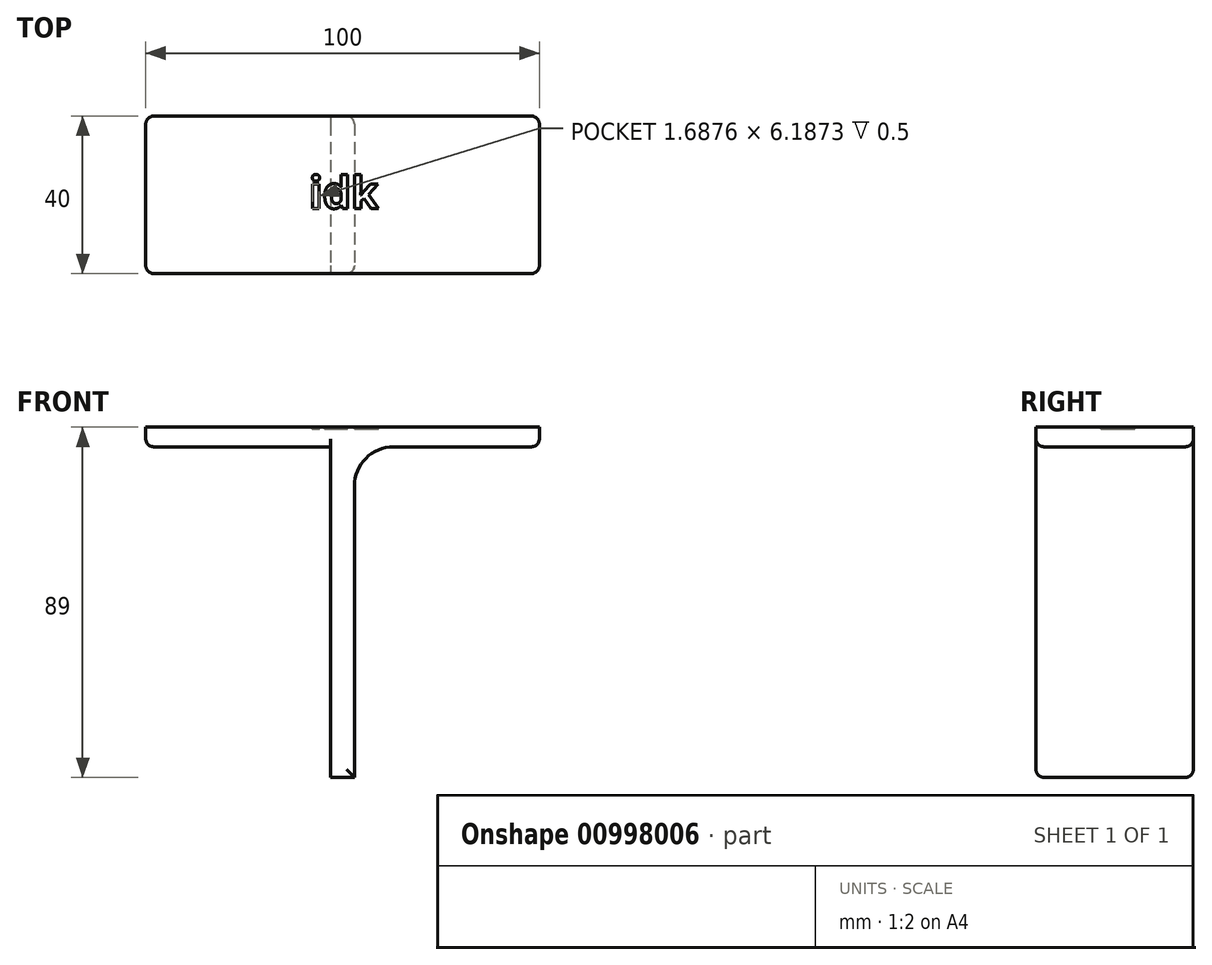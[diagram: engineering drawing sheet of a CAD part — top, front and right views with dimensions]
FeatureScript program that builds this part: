
annotation { "Feature Type Name" : "Feature", "Feature Type Description" : "" }
export const myFeature = defineFeature(function(context is Context, id is Id, definition is map)
    precondition{}
    {
        {
            var Q0;
            Q0=qCreatedBy(makeId("Top.planeOp"),FACE);
            var sketch = newSketch(context, id + "F0", { "sketchPlane" : qUnion([Q0])});
            skLineSegment(sketch, "E0.bottom", {"start": v(50, -20) * mm, "end": v(-50, -20) * mm});
            skLineSegment(sketch, "E0.top", {"start": v(50, 20) * mm, "end": v(-50, 20) * mm});
            skLineSegment(sketch, "E0.left", {"start": v(50, -20) * mm, "end": v(50, 20) * mm});
            skLineSegment(sketch, "E0.right", {"start": v(-50, -20) * mm, "end": v(-50, 20) * mm});
            skPoint(sketch, "E0.middle", {"position": v(0, 0) * mm});
            skLineSegment(sketch, "E1.bottom", {"start": v(-3, 20) * mm, "end": v(3, 20) * mm});
            skLineSegment(sketch, "E1.top", {"start": v(-3, -20) * mm, "end": v(3, -20) * mm});
            skLineSegment(sketch, "E1.left", {"start": v(-3, 20) * mm, "end": v(-3, -20) * mm});
            skLineSegment(sketch, "E1.right", {"start": v(3, 20) * mm, "end": v(3, -20) * mm});
            skSolve(sketch);
        }
        {
            var Q0;
            {var subQ2=sQuery(id+"F0.wireOp",EDGE,"E0.right");Q0=makeQuery(id+"F0.imprint","IMPRINT",FACE,{"disambiguationData":[TD([[makeQuery(id+"F0.imprint","IMPRINT",EDGE,{"derivedFrom":subQ2}),-1.0]])]});}
            var Q1;
            {var subQ0=sQuery(id+"F0.wireOp",EDGE,"E1.left");Q1=makeQuery(id+"F0.imprint","IMPRINT",FACE,{"disambiguationData":[TD([[makeQuery(id+"F0.imprint","IMPRINT",EDGE,{"derivedFrom":subQ0}),1.0]])]});}
            var Q2;
            {var subQ0=sQuery(id+"F0.wireOp",EDGE,"E0.left");Q2=makeQuery(id+"F0.imprint","IMPRINT",FACE,{"disambiguationData":[TD([[makeQuery(id+"F0.imprint","IMPRINT",EDGE,{"derivedFrom":subQ0}),1.0]])]});}
            extrude(context, id + "F1", {"entities" : qUnion([Q0, Q1, Q2]), "depth" : 5 * mm, "offsetDistance" : 25 * mm});
        }
        {
            var Q0;
            {var subQ0=sQuery(id+"F0.wireOp",EDGE,"E1.left");Q0=makeQuery(id+"F0.imprint","IMPRINT",FACE,{"disambiguationData":[TD([[makeQuery(id+"F0.imprint","IMPRINT",EDGE,{"derivedFrom":subQ0}),1.0]])]});}
            extrude(context, id + "F2", {"entities" : qUnion([Q0]), "operationType" : NewBodyOperationType.ADD, "oppositeDirection" : true, "depth" : 84 * mm, "offsetDistance" : 25 * mm});
        }
        {
            var Q0;
            Q0=makeQuery(id+"F2.opExtrude","CAP_EDGE",EDGE,{"disambiguationData":[OSD([sQuery(id+"F0.wireOp",EDGE,"E1.right")])],"isStart":true});
            var Q1;
            Q1=makeQuery(id+"F2.opExtrude","CAP_EDGE",EDGE,{"disambiguationData":[OSD([sQuery(id+"F0.wireOp",EDGE,"E1.left")])],"isStart":true});
            fillet(context, id + "F3", {"entities" : qUnion([Q0, Q1]), "radius" : 10 * mm, "tangentPropagation" : true, "allowEdgeOverflow" : false});
        }
        {
            var Q0;
            Q0=makeQuery(id+"F1.opExtrude","CAP_EDGE",EDGE,{"disambiguationData":[OSD([sQuery(id+"F0.wireOp",EDGE,"E0.right")])],"isStart":true});
            var Q1;
            {var subQ0=sQuery(id+"F0.wireOp",EDGE,"E0.top");var subQ1=sQuery(id+"F0.wireOp",EDGE,"E0.right");Q1=makeQuery(id+"F2.boolean.opBoolean","SPLIT",EDGE,{"disambiguationData":[TD([makeQuery(id+"F1.opExtrude","SWEPT_FACE",FACE,{"disambiguationData":[OSD([subQ1])]})])],"derivedFrom":makeQuery(id+"F1.opExtrude","CAP_EDGE",EDGE,{"disambiguationData":[OSD([subQ0])],"isStart":true})});}
            var Q2;
            Q2=makeQuery(id+"F1.opExtrude","SWEPT_EDGE",EDGE,{"disambiguationData":[OSD([sQuery(id+"F0.wireOp",EDGE,"E0.top"),sQuery(id+"F0.wireOp",EDGE,"E0.right")])]});
            var Q3;
            {var subQ0=sQuery(id+"F0.wireOp",EDGE,"E0.top");var subQ1=sQuery(id+"F0.wireOp",EDGE,"E0.left");Q3=makeQuery(id+"F2.boolean.opBoolean","SPLIT",EDGE,{"disambiguationData":[TD([makeQuery(id+"F1.opExtrude","SWEPT_FACE",FACE,{"disambiguationData":[OSD([subQ1])]})])],"derivedFrom":makeQuery(id+"F1.opExtrude","CAP_EDGE",EDGE,{"disambiguationData":[OSD([subQ0])],"isStart":true})});}
            var Q4;
            {var subQ0=sQuery(id+"F0.wireOp",EDGE,"E0.bottom");var subQ1=sQuery(id+"F0.wireOp",EDGE,"E0.right");Q4=makeQuery(id+"F2.boolean.opBoolean","SPLIT",EDGE,{"disambiguationData":[TD([makeQuery(id+"F1.opExtrude","SWEPT_FACE",FACE,{"disambiguationData":[OSD([subQ1])]})])],"derivedFrom":makeQuery(id+"F1.opExtrude","CAP_EDGE",EDGE,{"disambiguationData":[OSD([subQ0])],"isStart":true})});}
            var Q5;
            Q5=makeQuery(id+"F1.opExtrude","SWEPT_EDGE",EDGE,{"disambiguationData":[OSD([sQuery(id+"F0.wireOp",EDGE,"E0.bottom"),sQuery(id+"F0.wireOp",EDGE,"E0.right")])]});
            var Q6;
            {var subQ0=sQuery(id+"F0.wireOp",EDGE,"E0.left");var subQ1=sQuery(id+"F0.wireOp",EDGE,"E0.bottom");Q6=makeQuery(id+"F2.boolean.opBoolean","SPLIT",EDGE,{"disambiguationData":[TD([makeQuery(id+"F1.opExtrude","SWEPT_FACE",FACE,{"disambiguationData":[OSD([subQ0])]})])],"derivedFrom":makeQuery(id+"F1.opExtrude","CAP_EDGE",EDGE,{"disambiguationData":[OSD([subQ1])],"isStart":true})});}
            var Q7;
            Q7=makeQuery(id+"F1.opExtrude","SWEPT_EDGE",EDGE,{"disambiguationData":[OSD([sQuery(id+"F0.wireOp",EDGE,"E0.bottom"),sQuery(id+"F0.wireOp",EDGE,"E0.left")])]});
            var Q8;
            Q8=makeQuery(id+"F1.opExtrude","CAP_EDGE",EDGE,{"disambiguationData":[OSD([sQuery(id+"F0.wireOp",EDGE,"E0.left")])],"isStart":true});
            var Q9;
            Q9=makeQuery(id+"F1.opExtrude","SWEPT_EDGE",EDGE,{"disambiguationData":[OSD([sQuery(id+"F0.wireOp",EDGE,"E0.top"),sQuery(id+"F0.wireOp",EDGE,"E0.left")])]});
            var Q10;
            Q10=makeQuery(id+"F2.opExtrude","CAP_EDGE",EDGE,{"disambiguationData":[OSD([sQuery(id+"F0.wireOp",EDGE,"E0.top")])],"isStart":false});
            var Q11;
            Q11=makeQuery(id+"F2.opExtrude","CAP_EDGE",EDGE,{"disambiguationData":[OSD([sQuery(id+"F0.wireOp",EDGE,"E0.bottom")])],"isStart":false});
            fillet(context, id + "F4", {"entities" : qUnion([Q0, Q1, Q2, Q3, Q4, Q5, Q6, Q7, Q8, Q9, Q10, Q11]), "radius" : 2 * mm, "tangentPropagation" : true, "allowEdgeOverflow" : false});
        }
        {
            var Q0;
            Q0=makeQuery(id+"F1.opExtrude","CAP_FACE",FACE,{"disambiguationData":[OSD([sQuery(id+"F0.wireOp",EDGE,"E0.bottom"),sQuery(id+"F0.wireOp",EDGE,"E0.top"),sQuery(id+"F0.wireOp",EDGE,"E0.left"),sQuery(id+"F0.wireOp",EDGE,"E0.right")])],"isStart":false});
            var sketch = newSketch(context, id + "F5", { "sketchPlane" : qUnion([Q0])});
            skText(sketch, "E2", { "text": "idk", "fontName": "OpenSans-Bold.ttf"});
            const initialGuessF5  = {"E2": [-0.0085, -0.00344, 1, 0, 0.00816]};
            skSetInitialGuess(sketch, initialGuessF5);
            skSolve(sketch);
        }
        {
            var Q0;
            Q0 = qSketchRegion(id + "F5", true);
            extrude(context, id + "F6", {"entities" : qUnion([Q0]), "operationType" : NewBodyOperationType.REMOVE, "oppositeDirection" : true, "depth" : .5 * mm, "offsetDistance" : 25 * mm});
        }
    });
